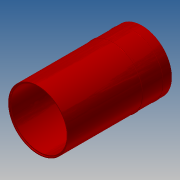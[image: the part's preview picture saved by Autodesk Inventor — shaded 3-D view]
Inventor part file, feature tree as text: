
AUTODESK INVENTOR PART (.ipt)
format: ipt  version: 2017.3 (Build 213257000, 257)  size: 173,568 bytes
history: native  units: in
note: dims shown in document units (in); Inventor stores cm internally (conversion verified against a paired STEP export)
features: extrude x5, sketch x5, fillet x3, plane x1, chamfer x1
ambient origin geometry x8: Origin, YZ Plane, XZ Plane, XY Plane, X Axis, Y Axis, Z Axis, Center Point
bodies: Solid1 (feature_tree)
feature tree (15):
  extrude  "Extrusion1"  Depth=30.5in
  extrude  "Extrusion2"  Depth=53.2283in
  fillet  "Fillet1"  Radius=4.5in
  plane  "Work Plane1"
  extrude  "Extrusion3"  [1 undecoded]
  extrude  "Extrusion4"  Depth=1.0in TaperAngle=0.0deg
  extrude  "Extrusion5"  Depth=0.0312in
  fillet  "Fillet2"  Radius=3.5in
  fillet  "Fillet3"  Radius=0.0312in
  chamfer  "Chamfer2"  Distance=29.5in
  sketch  "Sketch1"  dims[d0=28.5in d1=30.5in]
  sketch  "Sketch2"  dims[d2=53.2283in d3=0.0in d4=30.75in d5=4.5in d6=0.0in]
  sketch  "Sketch3"  dims[d7=0.1875in d11=-15.0394in]
  sketch  "Sketch4"  dims[d12=30.855in d13=1.0in d14=0.0in]
  sketch  "Sketch5"  dims[d15=0.1875in d16=30.516in d17=3.5in d18=0.0in d19=0.0312in d20=29.5in d21=0.5in d22=0.0in d23=0.0312in d24=0.125in d25=45.0deg]
note: 1 required parameter value undecoded (feature->parameter linkage not recoverable at this tier; creation-order binding heuristic only, values carry confidence <= 0.55)
